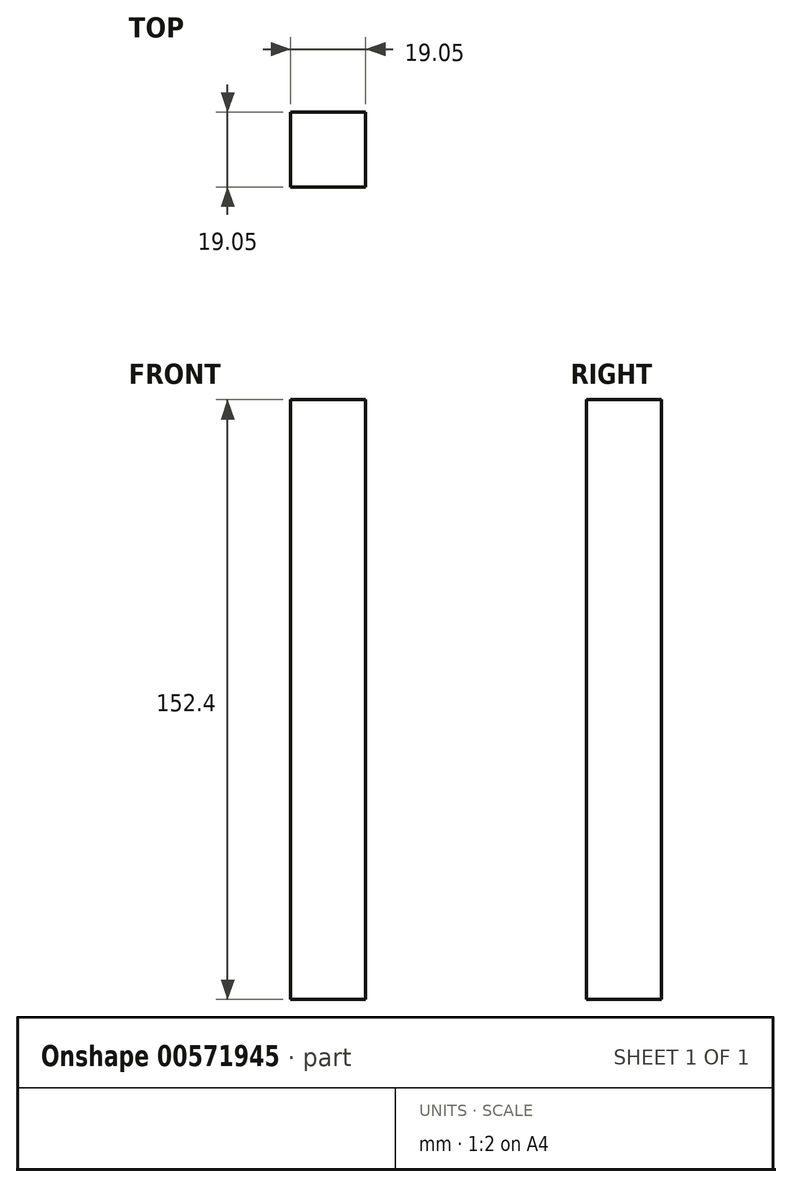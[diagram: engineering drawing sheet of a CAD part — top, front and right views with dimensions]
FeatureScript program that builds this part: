
annotation { "Feature Type Name" : "Feature", "Feature Type Description" : "" }
export const myFeature = defineFeature(function(context is Context, id is Id, definition is map)
    precondition{}
    {
        {
            var Q0;
            Q0=qCreatedBy(makeId("Top.planeOp"),FACE);
            var sketch = newSketch(context, id + "F0", { "sketchPlane" : qUnion([Q0])});
            skLineSegment(sketch, "E0.bottom", {"start": v(0, 0) * mm, "end": v(-19.05, 0) * mm});
            skLineSegment(sketch, "E0.top", {"start": v(0, -19.05) * mm, "end": v(-19.05, -19.05) * mm});
            skLineSegment(sketch, "E0.left", {"start": v(0, 0) * mm, "end": v(0, -19.05) * mm});
            skLineSegment(sketch, "E0.right", {"start": v(-19.05, 0) * mm, "end": v(-19.05, -19.05) * mm});
            skSolve(sketch);
        }
        {
            var Q0;
            Q0 = qSketchRegion(id + "F0", true);
            extrude(context, id + "F1", {"entities" : qUnion([Q0]), "depth" : 152.4 * mm, "offsetDistance" : 25.4 * mm});
        }
    });
